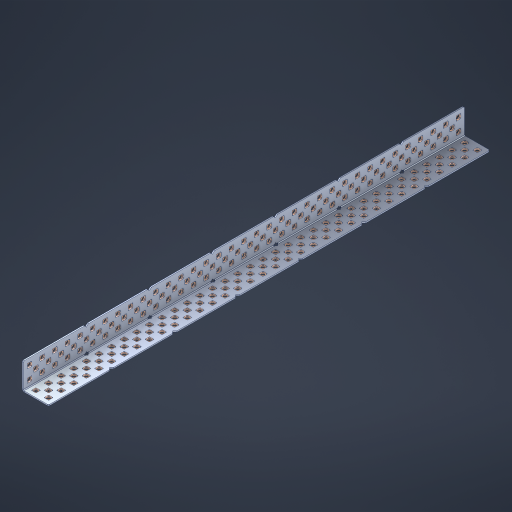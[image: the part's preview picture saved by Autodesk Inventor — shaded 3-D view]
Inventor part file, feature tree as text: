
AUTODESK INVENTOR PART (.ipt)
format: ipt  version: 2023 (Build 270158000, 158)  size: 2,292,736 bytes
history: native  units: in
note: dims shown in document units (in); Inventor stores cm internally (conversion verified against a paired STEP export)
features: other x214, extrude x206, sheet_metal_op x8, sketch x7, pattern_linear x2, mirror x1, chamfer x1
ambient origin geometry x8: Origin, YZ Plane, XZ Plane, XY Plane, X Axis, Y Axis, Z Axis, Center Point
bodies: Solid1 (feature_tree), Body (feature_tree)
feature tree (439):
  sheet_metal_op  "Flanges"
  sheet_metal_op  "Body Pattern"
  pattern_linear  "Center Pattern"  Spacing1=1.0in  [1 undecoded]
  other  "Arc Length"
  pattern_linear  "Notch Pattern"  Spacing1=0.1875in  [1 undecoded]
  other  "Diagonal Plane"
  mirror  "Everything Mirrored"
  chamfer  "End Chamfer"
  sketch  "Sketch1"  dims[d0=1.0in]
  other  "Plate1"
  sketch  "Sketch2"  dims[d1=17.5in]
  other  "Plate2"
  sheet_metal_op  "Bend1"
  sheet_metal_op  "Corner1"
  sketch  "Sketch8"  dims[d2=0.0469in]
  sketch  "Sketch9"  dims[d3=0.0469in]
  other  "Srf91"
  sheet_metal_op  "Body Pattern Sketch"
  other  "Srf92"
  sketch  "Sketch13"  dims[d4=0.0234in]
  sketch  "Sketch15"  dims[d5=0.0938in]
  sketch  "Sketch16"  dims[d6=0.0469in d7=1.0in d8=90.0deg d9=0.0312in d10=0.1875in d11=0.0469in d12=0.0469in d49=0.182in d50=0.02in d52=0.25in d53=0.0469in d54=0.0in d55=0.172in d56=1.0in d57=0.0in d60=13.7795in d62=0.5in d63=0.7874in d65=0.5in d85=0.1473in d86=0.1659in d89=0.0469in d90=0.0in d91=0.04in d92=0.0491in d95=2.5in d96=0.04in d97=0.25in d98=45.0deg d99=0.25in d106=0.182in d107=0.02in d108=0.5in d110=0.0469in d111=0.0in d112=0.172in d113=0.5in d114=0.0in d117=0.5in d123=0.25in d125=0.25in d126=0.0491in d127=0.1227in d128=0.08in d129=0.04in d130=2.5in]
  other  "Srf786"
  other  "Srf856"
  other  "Srf857"
  other  "Srf858"
  other  "Srf859"
  other  "Srf860"
  other  "Srf861"
  other  "Srf889"
  other  "Srf890"
  other  "Srf891"
  other  "Srf1275"
  other  "Srf1276"
  other  "Srf1278"
  other  "Srf1279"
  other  "Srf1280"
  other  "Srf1281"
  other  "Srf1282"
  other  "Srf1283"
  other  "Srf1277"
  other  "Srf1285"
  other  "Srf1286"
  other  "Srf1287"
  other  "Srf1383"
  other  "Srf1384"
  other  "Srf1385"
  other  "Srf1386"
  other  "Srf1387"
  other  "Srf1388"
  other  "Srf1389"
  other  "Srf1390"
  other  "Srf1391"
  other  "Srf1392"
  other  "Srf1393"
  other  "Srf1394"
  other  "Srf1395"
  other  "Srf1396"
  other  "Srf1397"
  other  "Srf1398"
  other  "Srf1399"
  other  "Srf1400"
  other  "Srf1401"
  other  "Srf1402"
  other  "Srf1403"
  other  "Srf1404"
  other  "Srf1405"
  other  "Srf1406"
  other  "Srf1407"
  other  "Srf1408"
  other  "Srf1409"
  other  "Srf1410"
  other  "Srf1411"
  other  "Srf1412"
  other  "Srf1413"
  other  "Srf1414"
  other  "Srf1415"
  other  "Srf1416"
  other  "Srf1417"
  other  "Srf1418"
  other  "Srf1419"
  other  "Srf1420"
  other  "Srf1421"
  other  "Srf1422"
  other  "Srf1423"
  other  "Srf1424"
  other  "Srf1425"
  other  "Srf1426"
  other  "Srf1427"
  other  "Srf1428"
  other  "Srf1429"
  other  "Srf1430"
  other  "Srf1431"
  other  "Srf1432"
  other  "Srf1433"
  other  "Srf1434"
  other  "Srf1435"
  other  "Srf1436"
  other  "Srf1437"
  other  "Srf1438"
  other  "Srf1439"
  other  "Srf1440"
  other  "Srf1441"
  other  "Srf1442"
  other  "Srf1443"
  other  "Srf1444"
  other  "Srf1445"
  other  "Srf1446"
  other  "Srf1447"
  other  "Srf1448"
  other  "Srf1449"
  other  "Srf1450"
  other  "Srf1451"
  other  "Srf1452"
  other  "Srf1453"
  other  "Srf1454"
  other  "Srf1455"
  other  "Srf1456"
  other  "Srf1457"
  other  "Srf1458"
  other  "Srf1459"
  other  "Srf1460"
  other  "Srf1461"
  other  "Srf1462"
  other  "Srf1463"
  other  "Srf1464"
  other  "Srf1465"
  other  "Srf1466"
  other  "Srf1467"
  other  "Srf1468"
  other  "Srf1469"
  other  "Srf1470"
  other  "Srf1471"
  other  "Srf1472"
  other  "Srf1473"
  other  "Srf1474"
  other  "Srf1475"
  other  "Srf1476"
  other  "Srf1477"
  other  "Srf1478"
  other  "Srf1479"
  other  "Srf1480"
  other  "Srf1481"
  other  "Srf1482"
  other  "Srf1483"
  other  "Srf1484"
  other  "Srf1485"
  other  "Srf1486"
  other  "Srf1487"
  other  "Srf1488"
  other  "Srf1489"
  other  "Srf1490"
  other  "Srf1491"
  other  "Srf1492"
  other  "Srf1493"
  other  "Srf1494"
  other  "Srf1495"
  other  "Srf1496"
  other  "Srf1497"
  other  "Srf1498"
  other  "Srf1499"
  other  "Srf1500"
  other  "Srf1501"
  other  "Srf1502"
  other  "Srf1503"
  other  "Srf1504"
  other  "Srf1505"
  other  "Srf1506"
  other  "Srf1507"
  other  "Srf1508"
  other  "Srf1509"
  other  "Srf1510"
  other  "Srf1511"
  other  "Srf1512"
  other  "Srf1513"
  other  "Srf1514"
  other  "Srf1515"
  other  "Srf1516"
  other  "Srf1517"
  other  "Srf1518"
  other  "Srf1519"
  other  "Srf1520"
  other  "Srf1521"
  other  "Srf1522"
  other  "Srf1523"
  other  "Srf1524"
  other  "Srf1525"
  other  "Srf1526"
  other  "Srf1527"
  other  "Srf1528"
  other  "Srf1529"
  other  "Srf1530"
  other  "Srf1531"
  other  "Srf1532"
  other  "Srf1533"
  other  "Srf1534"
  other  "Srf1535"
  other  "Srf1536"
  other  "Srf1537"
  other  "Srf1538"
  other  "Srf1539"
  other  "Srf1540"
  other  "Srf1541"
  other  "Srf1542"
  other  "Srf1543"
  other  "Srf1544"
  other  "Srf1545"
  other  "Srf1546"
  other  "Srf1547"
  other  "Srf1548"
  other  "Srf1549"
  other  "Srf1550"
  other  "Srf1551"
  other  "Srf1552"
  other  "Srf1553"
  other  "Srf1554"
  other  "Srf1555"
  other  "Srf1556"
  other  "Srf1557"
  other  "Srf1558"
  other  "Srf1559"
  other  "Srf1560"
  other  "Srf1561"
  other  "Srf1562"
  other  "Srf1563"
  other  "Srf1564"
  other  "Srf1565"
  other  "Srf1566"
  sheet_metal_op  "Body Stamp"
  sheet_metal_op  "Body Circle"
  other  "Center Stamp"
  other  "Center Circle"
  sheet_metal_op  "Notch"
  extrude  "ExtrusionSrf92"  Depth=0.0469in
  extrude  "ExtrusionSrf856"  Depth=0.0469in
  extrude  "ExtrusionSrf857"  Depth=2.5in
  extrude  "ExtrusionSrf858"  Depth=0.02in
  extrude  "ExtrusionSrf859"  Depth=2.5in
  extrude  "ExtrusionSrf860"  Depth=0.0469in
  extrude  "ExtrusionSrf861"  TaperAngle=0.0deg  [1 undecoded]
  extrude  "ExtrusionSrf889"  Depth=2.5in
  extrude  "ExtrusionSrf890"  Depth=1.0in TaperAngle=0.0deg
  extrude  "ExtrusionSrf891"  Depth=2.5in
  extrude  "ExtrusionSrf1275"  Depth=0.5in
  extrude  "ExtrusionSrf1276"  Depth=2.5in
  extrude  "ExtrusionSrf1277"  Depth=2.5in
  extrude  "ExtrusionSrf1278"  Depth=0.0469in
  extrude  "ExtrusionSrf1279"  Depth=2.5in TaperAngle=0.0deg
  extrude  "ExtrusionSrf1280"  Depth=2.5in
  extrude  "ExtrusionSrf1281"  Depth=2.5in TaperAngle=45.0deg
  extrude  "ExtrusionSrf1282"  Depth=2.5in
  extrude  "ExtrusionSrf1345"  Depth=2.5in
  extrude  "ExtrusionSrf1346"  Depth=0.02in
  extrude  "ExtrusionSrf1347"  Depth=0.5in
  extrude  "ExtrusionSrf1348"  Depth=0.0469in
  extrude  "ExtrusionSrf1383"  TaperAngle=0.0deg  [1 undecoded]
  extrude  "ExtrusionSrf1384"  Depth=2.5in
  extrude  "ExtrusionSrf1385"  Depth=0.5in TaperAngle=0.0deg
  extrude  "ExtrusionSrf1386"  Depth=0.5in
  extrude  "ExtrusionSrf1387"  Depth=2.5in
  extrude  "ExtrusionSrf1388"  Depth=2.5in
  extrude  "ExtrusionSrf1389"  Depth=2.5in
  extrude  "ExtrusionSrf1390"  Depth=2.5in
  extrude  "ExtrusionSrf1391"  Depth=2.5in
  extrude  "ExtrusionSrf1392"  Depth=2.5in
  extrude  "ExtrusionSrf1393"  Depth=2.5in
  extrude  "ExtrusionSrf1394"  [1 undecoded]
  extrude  "ExtrusionSrf1395"  [1 undecoded]
  extrude  "ExtrusionSrf1396"  [1 undecoded]
  extrude  "ExtrusionSrf1397"  [1 undecoded]
  extrude  "ExtrusionSrf1398"  [1 undecoded]
  extrude  "ExtrusionSrf1399"  [1 undecoded]
  extrude  "ExtrusionSrf1400"  [1 undecoded]
  extrude  "ExtrusionSrf1401"  [1 undecoded]
  extrude  "ExtrusionSrf1402"  [1 undecoded]
  extrude  "ExtrusionSrf1403"  [1 undecoded]
  extrude  "ExtrusionSrf1404"  [1 undecoded]
  extrude  "ExtrusionSrf1405"  [1 undecoded]
  extrude  "ExtrusionSrf1406"  [1 undecoded]
  extrude  "ExtrusionSrf1407"  [1 undecoded]
  extrude  "ExtrusionSrf1408"  [1 undecoded]
  extrude  "ExtrusionSrf1409"  [1 undecoded]
  extrude  "ExtrusionSrf1410"  [1 undecoded]
  extrude  "ExtrusionSrf1411"  [1 undecoded]
  extrude  "ExtrusionSrf1412"  [1 undecoded]
  extrude  "ExtrusionSrf1413"  [1 undecoded]
  extrude  "ExtrusionSrf1414"  [1 undecoded]
  extrude  "ExtrusionSrf1415"  [1 undecoded]
  extrude  "ExtrusionSrf1416"  [1 undecoded]
  extrude  "ExtrusionSrf1417"  [1 undecoded]
  extrude  "ExtrusionSrf1418"  [1 undecoded]
  extrude  "ExtrusionSrf1419"  [1 undecoded]
  extrude  "ExtrusionSrf1420"  [1 undecoded]
  extrude  "ExtrusionSrf1421"  [1 undecoded]
  extrude  "ExtrusionSrf1422"  [1 undecoded]
  extrude  "ExtrusionSrf1423"  [1 undecoded]
  extrude  "ExtrusionSrf1424"  [1 undecoded]
  extrude  "ExtrusionSrf1425"  [1 undecoded]
  extrude  "ExtrusionSrf1426"  [1 undecoded]
  extrude  "ExtrusionSrf1427"  [1 undecoded]
  extrude  "ExtrusionSrf1428"  [1 undecoded]
  extrude  "ExtrusionSrf1429"  [1 undecoded]
  extrude  "ExtrusionSrf1430"  [1 undecoded]
  extrude  "ExtrusionSrf1431"  [1 undecoded]
  extrude  "ExtrusionSrf1432"  [1 undecoded]
  extrude  "ExtrusionSrf1433"  [1 undecoded]
  extrude  "ExtrusionSrf1434"  [1 undecoded]
  extrude  "ExtrusionSrf1435"  [1 undecoded]
  extrude  "ExtrusionSrf1436"  [1 undecoded]
  extrude  "ExtrusionSrf1437"  [1 undecoded]
  extrude  "ExtrusionSrf1438"  [1 undecoded]
  extrude  "ExtrusionSrf1439"  [1 undecoded]
  extrude  "ExtrusionSrf1440"  [1 undecoded]
  extrude  "ExtrusionSrf1441"  [1 undecoded]
  extrude  "ExtrusionSrf1442"  [1 undecoded]
  extrude  "ExtrusionSrf1443"  [1 undecoded]
  extrude  "ExtrusionSrf1444"  [1 undecoded]
  extrude  "ExtrusionSrf1445"  [1 undecoded]
  extrude  "ExtrusionSrf1446"  [1 undecoded]
  extrude  "ExtrusionSrf1447"  [1 undecoded]
  extrude  "ExtrusionSrf1448"  [1 undecoded]
  extrude  "ExtrusionSrf1449"  [1 undecoded]
  extrude  "ExtrusionSrf1450"  [1 undecoded]
  extrude  "ExtrusionSrf1451"  [1 undecoded]
  extrude  "ExtrusionSrf1452"  [1 undecoded]
  extrude  "ExtrusionSrf1453"  [1 undecoded]
  extrude  "ExtrusionSrf1454"  [1 undecoded]
  extrude  "ExtrusionSrf1455"  [1 undecoded]
  extrude  "ExtrusionSrf1456"  [1 undecoded]
  extrude  "ExtrusionSrf1457"  [1 undecoded]
  extrude  "ExtrusionSrf1458"  [1 undecoded]
  extrude  "ExtrusionSrf1459"  [1 undecoded]
  extrude  "ExtrusionSrf1460"  [1 undecoded]
  extrude  "ExtrusionSrf1461"  [1 undecoded]
  extrude  "ExtrusionSrf1462"  [1 undecoded]
  extrude  "ExtrusionSrf1463"  [1 undecoded]
  extrude  "ExtrusionSrf1464"  [1 undecoded]
  extrude  "ExtrusionSrf1465"  [1 undecoded]
  extrude  "ExtrusionSrf1466"  [1 undecoded]
  extrude  "ExtrusionSrf1467"  [1 undecoded]
  extrude  "ExtrusionSrf1468"  [1 undecoded]
  extrude  "ExtrusionSrf1469"  [1 undecoded]
  extrude  "ExtrusionSrf1470"  [1 undecoded]
  extrude  "ExtrusionSrf1471"  [1 undecoded]
  extrude  "ExtrusionSrf1472"  [1 undecoded]
  extrude  "ExtrusionSrf1473"  [1 undecoded]
  extrude  "ExtrusionSrf1474"  [1 undecoded]
  extrude  "ExtrusionSrf1475"  [1 undecoded]
  extrude  "ExtrusionSrf1476"  [1 undecoded]
  extrude  "ExtrusionSrf1477"  [1 undecoded]
  extrude  "ExtrusionSrf1478"  [1 undecoded]
  extrude  "ExtrusionSrf1479"  [1 undecoded]
  extrude  "ExtrusionSrf1480"  [1 undecoded]
  extrude  "ExtrusionSrf1481"  [1 undecoded]
  extrude  "ExtrusionSrf1482"  [1 undecoded]
  extrude  "ExtrusionSrf1483"  [1 undecoded]
  extrude  "ExtrusionSrf1484"  [1 undecoded]
  extrude  "ExtrusionSrf1485"  [1 undecoded]
  extrude  "ExtrusionSrf1486"  [1 undecoded]
  extrude  "ExtrusionSrf1487"  [1 undecoded]
  extrude  "ExtrusionSrf1488"  [1 undecoded]
  extrude  "ExtrusionSrf1489"  [1 undecoded]
  extrude  "ExtrusionSrf1490"  [1 undecoded]
  extrude  "ExtrusionSrf1491"  [1 undecoded]
  extrude  "ExtrusionSrf1492"  [1 undecoded]
  extrude  "ExtrusionSrf1493"  [1 undecoded]
  extrude  "ExtrusionSrf1494"  [1 undecoded]
  extrude  "ExtrusionSrf1495"  [1 undecoded]
  extrude  "ExtrusionSrf1496"  [1 undecoded]
  extrude  "ExtrusionSrf1497"  [1 undecoded]
  extrude  "ExtrusionSrf1498"  [1 undecoded]
  extrude  "ExtrusionSrf1499"  [1 undecoded]
  extrude  "ExtrusionSrf1500"  [1 undecoded]
  extrude  "ExtrusionSrf1501"  [1 undecoded]
  extrude  "ExtrusionSrf1502"  [1 undecoded]
  extrude  "ExtrusionSrf1503"  [1 undecoded]
  extrude  "ExtrusionSrf1504"  [1 undecoded]
  extrude  "ExtrusionSrf1505"  [1 undecoded]
  extrude  "ExtrusionSrf1506"  [1 undecoded]
  extrude  "ExtrusionSrf1507"  [1 undecoded]
  extrude  "ExtrusionSrf1508"  [1 undecoded]
  extrude  "ExtrusionSrf1509"  [1 undecoded]
  extrude  "ExtrusionSrf1510"  [1 undecoded]
  extrude  "ExtrusionSrf1511"  [1 undecoded]
  extrude  "ExtrusionSrf1512"  [1 undecoded]
  extrude  "ExtrusionSrf1513"  [1 undecoded]
  extrude  "ExtrusionSrf1514"  [1 undecoded]
  extrude  "ExtrusionSrf1515"  [1 undecoded]
  extrude  "ExtrusionSrf1516"  [1 undecoded]
  extrude  "ExtrusionSrf1517"  [1 undecoded]
  extrude  "ExtrusionSrf1518"  [1 undecoded]
  extrude  "ExtrusionSrf1519"  [1 undecoded]
  extrude  "ExtrusionSrf1520"  [1 undecoded]
  extrude  "ExtrusionSrf1521"  [1 undecoded]
  extrude  "ExtrusionSrf1522"  [1 undecoded]
  extrude  "ExtrusionSrf1523"  [1 undecoded]
  extrude  "ExtrusionSrf1524"  [1 undecoded]
  extrude  "ExtrusionSrf1525"  [1 undecoded]
  extrude  "ExtrusionSrf1526"  [1 undecoded]
  extrude  "ExtrusionSrf1527"  [1 undecoded]
  extrude  "ExtrusionSrf1528"  [1 undecoded]
  extrude  "ExtrusionSrf1529"  [1 undecoded]
  extrude  "ExtrusionSrf1530"  [1 undecoded]
  extrude  "ExtrusionSrf1531"  [1 undecoded]
  extrude  "ExtrusionSrf1532"  [1 undecoded]
  extrude  "ExtrusionSrf1533"  [1 undecoded]
  extrude  "ExtrusionSrf1534"  [1 undecoded]
  extrude  "ExtrusionSrf1535"  [1 undecoded]
  extrude  "ExtrusionSrf1536"  [1 undecoded]
  extrude  "ExtrusionSrf1537"  [1 undecoded]
  extrude  "ExtrusionSrf1538"  [1 undecoded]
  extrude  "ExtrusionSrf1539"  [1 undecoded]
  extrude  "ExtrusionSrf1540"  [1 undecoded]
  extrude  "ExtrusionSrf1541"  [1 undecoded]
  extrude  "ExtrusionSrf1542"  [1 undecoded]
  extrude  "ExtrusionSrf1543"  [1 undecoded]
  extrude  "ExtrusionSrf1544"  [1 undecoded]
  extrude  "ExtrusionSrf1545"  [1 undecoded]
  extrude  "ExtrusionSrf1546"  [1 undecoded]
  extrude  "ExtrusionSrf1547"  [1 undecoded]
  extrude  "ExtrusionSrf1548"  [1 undecoded]
  extrude  "ExtrusionSrf1549"  [1 undecoded]
  extrude  "ExtrusionSrf1550"  [1 undecoded]
  extrude  "ExtrusionSrf1551"  [1 undecoded]
  extrude  "ExtrusionSrf1552"  [1 undecoded]
  extrude  "ExtrusionSrf1553"  [1 undecoded]
  extrude  "ExtrusionSrf1554"  [1 undecoded]
  extrude  "ExtrusionSrf1555"  [1 undecoded]
  extrude  "ExtrusionSrf1556"  [1 undecoded]
  extrude  "ExtrusionSrf1557"  [1 undecoded]
  extrude  "ExtrusionSrf1558"  [1 undecoded]
  extrude  "ExtrusionSrf1559"  [1 undecoded]
  extrude  "ExtrusionSrf1560"  [1 undecoded]
  extrude  "ExtrusionSrf1561"  [1 undecoded]
  extrude  "ExtrusionSrf1562"  [1 undecoded]
  extrude  "ExtrusionSrf1563"  [1 undecoded]
  extrude  "ExtrusionSrf1564"  [1 undecoded]
  extrude  "ExtrusionSrf1565"  [1 undecoded]
  extrude  "ExtrusionSrf1566"  [1 undecoded]
note: 177 required parameter values undecoded (feature->parameter linkage not recoverable at this tier; creation-order binding heuristic only, values carry confidence <= 0.55)
